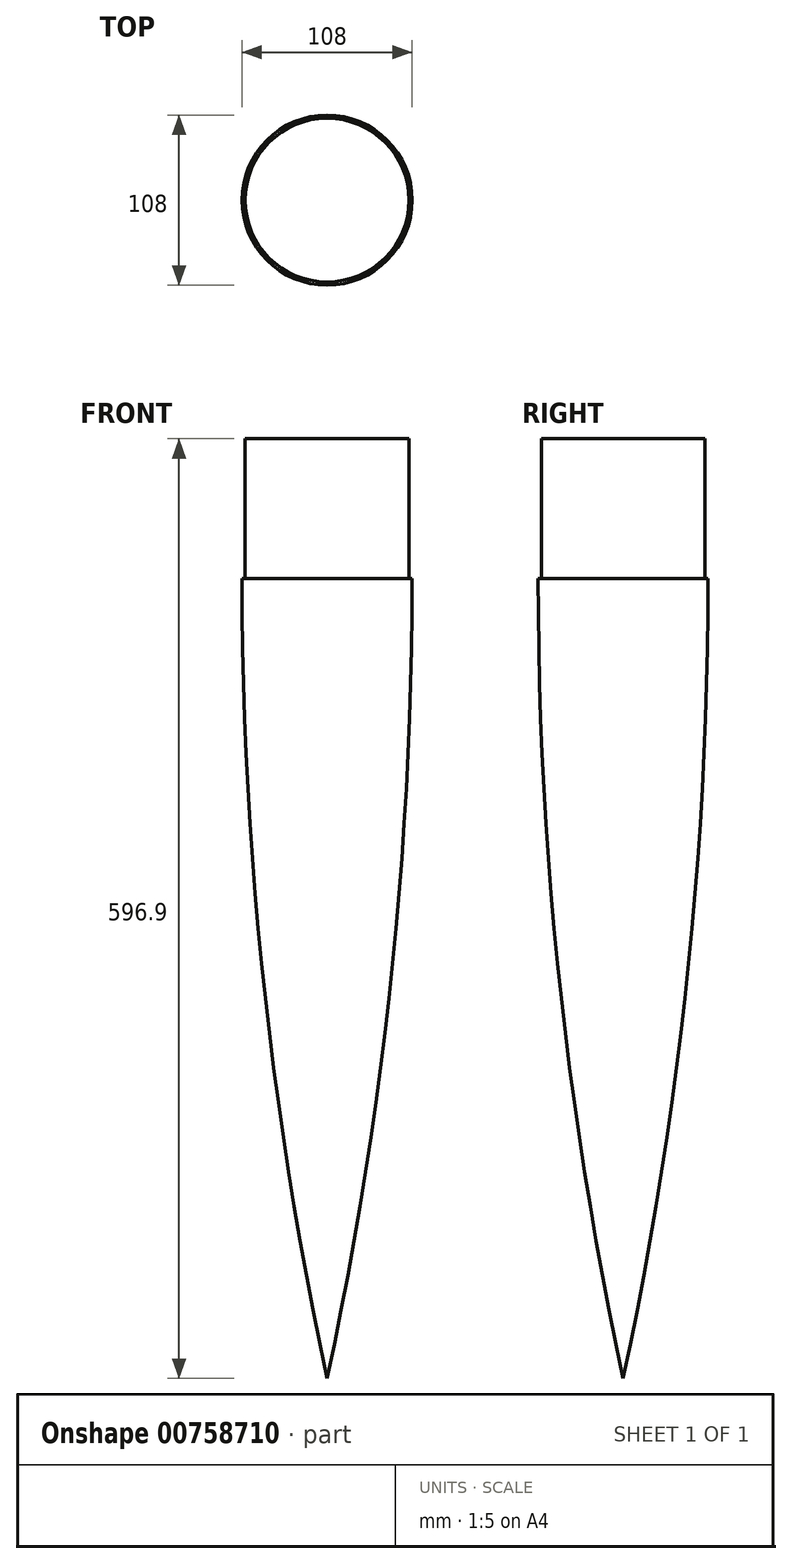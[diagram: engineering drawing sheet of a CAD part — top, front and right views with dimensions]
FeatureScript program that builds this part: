
annotation { "Feature Type Name" : "Feature", "Feature Type Description" : "" }
export const myFeature = defineFeature(function(context is Context, id is Id, definition is map)
    precondition{}
    {
        {
            var Q0;
            Q0=qCreatedBy(makeId("Front.planeOp"),FACE);
            var sketch = newSketch(context, id + "F0", { "sketchPlane" : qUnion([Q0])});
            skLineSegment(sketch, "E0", {"start": v(0, 0) * mm, "end": v(0, 508) * mm});
            skLineSegment(sketch, "E1", {"start": v(0, 0) * mm, "end": v(0, -508) * mm});
            skLineSegment(sketch, "E2", {"start": v(0, 0) * mm, "end": v(54, 0) * mm});
            skArc(sketch, "E3", {"start": v(0, -508) * mm, "mid": v(54, 0) * mm, "end": v(0, 508) * mm});
            skSolve(sketch);
        }
        {
            var Q0;
            Q0=qCreatedBy(makeId("Top.planeOp"),FACE);
            var sketch = newSketch(context, id + "F1", { "sketchPlane" : qUnion([Q0])});
            skCircle(sketch, "E4", {"center": v(0, 0) * mm, "radius": 54 * mm});
            skSolve(sketch);
        }
        {
            var Q0;
            {var subQ0=sQuery(id+"F0.wireOp",EDGE,"E1");Q0=makeQuery(id+"F0.imprint","IMPRINT",FACE,{"disambiguationData":[TD([[makeQuery(id+"F0.imprint","IMPRINT",EDGE,{"derivedFrom":subQ0}),1.0]])]});}
            var Q1;
            Q1=sQuery(id+"F1.wireOp",EDGE,"E4");
            revolve(context, id + "F2", {"surfaceOperationType" : NewSurfaceOperationType.NEW, "entities" : qUnion([Q0]), "axis" : qUnion([Q1]), "revolveType" : RevolveType.SYMMETRIC, "angle" : 360 * degree});
        }
        {
            var Q0;
            Q0=makeQuery(id+"F2.opRevolve","SWEPT_FACE",FACE,{"disambiguationData":[OSD([sQuery(id+"F0.wireOp",EDGE,"E2")])]});
            var sketch = newSketch(context, id + "F3", { "sketchPlane" : qUnion([Q0])});
            skCircle(sketch, "E5", {"center": v(0, 0) * mm, "radius": 52 * mm});
            skSolve(sketch);
        }
        {
            var Q0;
            Q0=makeQuery(id+"F3.imprint","IMPRINT",FACE,{"disambiguationData":[TD([[makeQuery(id+"F3.imprint","IMPRINT",EDGE,{"derivedFrom":sQuery(id+"F3.wireOp",EDGE,"E5")}),1.0]])]});
            extrude(context, id + "F4", {"entities" : qUnion([Q0]), "operationType" : NewBodyOperationType.ADD, "depth" : 25.4 * mm, "offsetDistance" : 25.4 * mm});
        }
        {
            var Q0;
            Q0=makeQuery(id+"F4.opExtrude","CAP_FACE",FACE,{"disambiguationData":[OSD([sQuery(id+"F3.wireOp",EDGE,"E5")])],"isStart":false});
            extrude(context, id + "F5", {"entities" : qUnion([Q0]), "operationType" : NewBodyOperationType.ADD, "depth" : 63.5 * mm, "offsetDistance" : 25.4 * mm});
        }
    });
